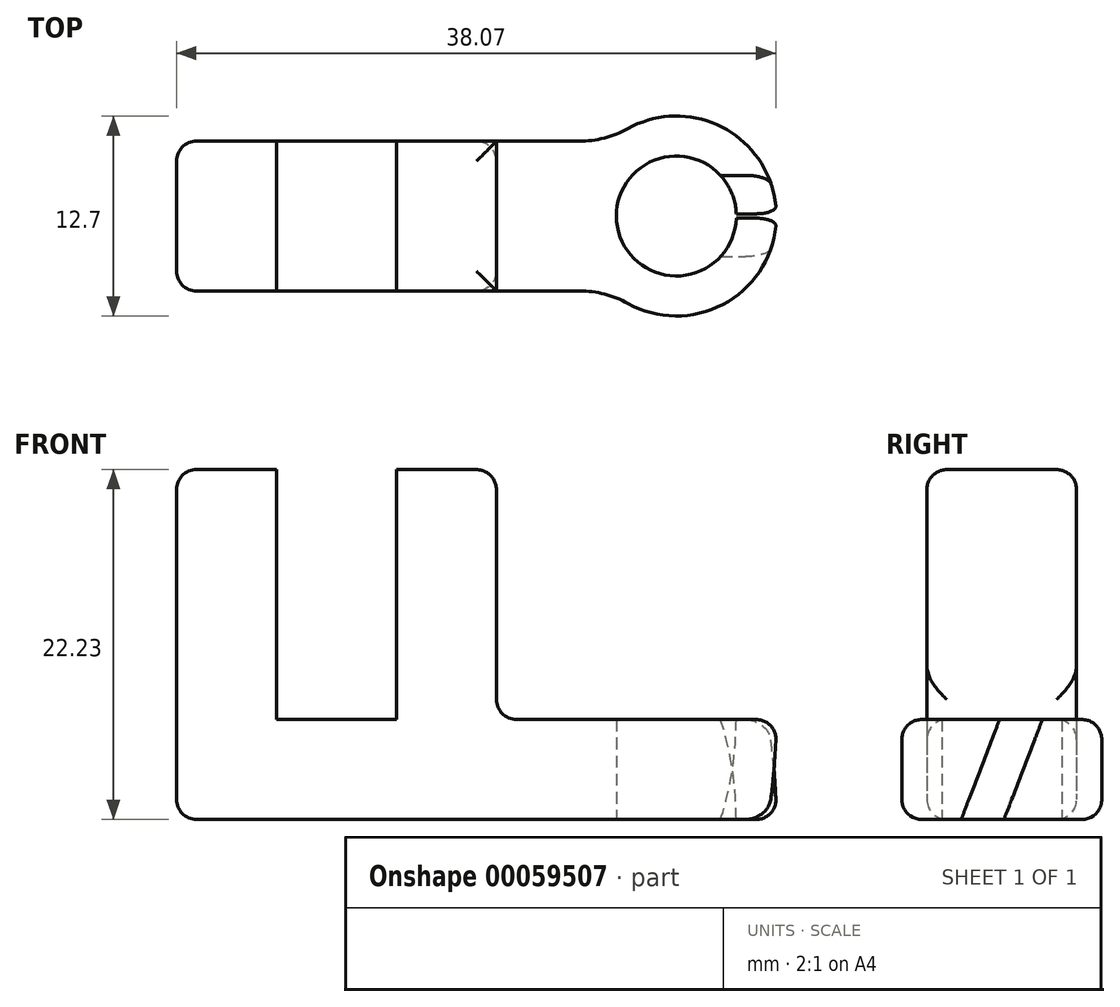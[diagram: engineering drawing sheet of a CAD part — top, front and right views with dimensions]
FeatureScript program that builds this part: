
annotation { "Feature Type Name" : "Feature", "Feature Type Description" : "" }
export const myFeature = defineFeature(function(context is Context, id is Id, definition is map)
    precondition{}
    {
        {
            var Q0;
            Q0=qCreatedBy(makeId("Top.planeOp"),FACE);
            var sketch = newSketch(context, id + "F0", { "sketchPlane" : qUnion([Q0])});
            skArc(sketch, "E0", {"start": v(-3.07, -5.56) * mm, "mid": v(6.35, 0) * mm, "end": v(-3.09, 5.55) * mm});
            skCircle(sketch, "E1", {"center": v(0, 0) * mm, "radius": 3.81 * mm});
            skLineSegment(sketch, "E2", {"start": v(0, 0) * mm, "end": v(-31.75, 0) * mm, "construction": true});
            skLineSegment(sketch, "E3.0", {"start": v(-6.17, 4.75) * mm, "end": v(-31.75, 4.75) * mm});
            skLineSegment(sketch, "E4.0", {"start": v(-6.15, -4.76) * mm, "end": v(-31.75, -4.76) * mm});
            skLineSegment(sketch, "E5", {"start": v(-31.75, 4.75) * mm, "end": v(-31.75, -4.76) * mm});
            skPoint(sketch, "E6.visualSharp", {"position": v(-4.21, 4.75) * mm});
            skArc(sketch, "E6.filletArc", {"start": v(-6.17, 4.75) * mm, "mid": v(-4.58, 4.95) * mm, "end": v(-3.09, 5.55) * mm});
            skPoint(sketch, "E7.visualSharp", {"position": v(-4.2, -4.76) * mm});
            skArc(sketch, "E7.filletArc", {"start": v(-3.07, -5.56) * mm, "mid": v(-4.56, -4.96) * mm, "end": v(-6.15, -4.76) * mm});
            skSolve(sketch);
        }
        {
            var Q0;
            Q0=makeQuery(id+"F0.imprint","IMPRINT",FACE,{"disambiguationData":[TD([[makeQuery(id+"F0.imprint","IMPRINT",EDGE,{"derivedFrom":sQuery(id+"F0.wireOp",EDGE,"E0")}),1.0]])]});
            extrude(context, id + "F1", {"entities" : qUnion([Q0]), "depth" : 6.35 * mm});
        }
        {
            var Q0;
            Q0=makeQuery(id+"F1.opExtrude","CAP_FACE",FACE,{"disambiguationData":[OSD([sQuery(id+"F0.wireOp",EDGE,"E0"),sQuery(id+"F0.wireOp",EDGE,"E1"),sQuery(id+"F0.wireOp",EDGE,"E3.0"),sQuery(id+"F0.wireOp",EDGE,"E4.0"),sQuery(id+"F0.wireOp",EDGE,"E5"),sQuery(id+"F0.wireOp",EDGE,"E6.filletArc"),sQuery(id+"F0.wireOp",EDGE,"E7.filletArc")])],"isStart":false});
            var sketch = newSketch(context, id + "F2", { "sketchPlane" : qUnion([Q0])});
            skLineSegment(sketch, "E8.0", {"start": v(-25.4, 4.75) * mm, "end": v(-25.4, -4.76) * mm});
            skLineSegment(sketch, "E9.0", {"start": v(-17.78, 4.75) * mm, "end": v(-17.78, -4.76) * mm});
            skLineSegment(sketch, "E10.0", {"start": v(-11.43, 4.75) * mm, "end": v(-11.43, -4.76) * mm});
            skSolve(sketch);
        }
        {
            var Q0;
            {var subQ0=sQuery(id+"F2.wireOp",EDGE,"E8.0");Q0=makeQuery(id+"F2.imprint","IMPRINT",FACE,{"disambiguationData":[TD([[makeQuery(id+"F2.imprint","IMPRINT",EDGE,{"derivedFrom":subQ0}),-1.0]])]});}
            var Q1;
            {var subQ0=sQuery(id+"F2.wireOp",EDGE,"E9.0");Q1=makeQuery(id+"F2.imprint","IMPRINT",FACE,{"disambiguationData":[TD([[makeQuery(id+"F2.imprint","IMPRINT",EDGE,{"derivedFrom":subQ0}),1.0]])]});}
            extrude(context, id + "F3", {"entities" : qUnion([Q0, Q1]), "operationType" : NewBodyOperationType.ADD, "depth" : 15.88 * mm});
        }
        {
            var Q0;
            Q0=makeQuery(id+"F1.opExtrude","CAP_EDGE",EDGE,{"disambiguationData":[OSD([sQuery(id+"F0.wireOp",EDGE,"E4.0")])],"isStart":true});
            var Q1;
            {var subQ1=sQuery(id+"F0.wireOp",EDGE,"E4.0");var subQ2=makeQuery(id+"F1.opExtrude","CAP_EDGE",EDGE,{"disambiguationData":[OSD([subQ1])],"isStart":false});var subQ3=sQuery(id+"F0.wireOp",EDGE,"E7.filletArc");Q1=makeQuery(id+"F3.boolean.opBoolean","SPLIT",EDGE,{"disambiguationData":[TD([makeQuery(id+"F1.opExtrude","SWEPT_FACE",FACE,{"disambiguationData":[OSD([subQ3])]})])],"derivedFrom":subQ2});}
            var Q2;
            Q2=makeQuery(id+"F3.opExtrude","CAP_EDGE",EDGE,{"disambiguationData":[OSD([sQuery(id+"F2.wireOp",EDGE,"E10.0")])],"isStart":true});
            var Q3;
            Q3=makeQuery(id+"F3.opExtrude","CAP_EDGE",EDGE,{"disambiguationData":[OSD([sQuery(id+"F2.wireOp",EDGE,"E10.0")])],"isStart":false});
            var Q4;
            {var subQ0=sQuery(id+"F0.wireOp",EDGE,"E5");var subQ1=sQuery(id+"F0.wireOp",EDGE,"E4.0");Q4=makeQuery(id+"F3.boolean.opBoolean","MERGE",EDGE,{"derivedFrom":[makeQuery(id+"F1.opExtrude","SWEPT_EDGE",EDGE,{"disambiguationData":[OSD([subQ1,subQ0])]}),makeQuery(id+"F3.opExtrude","SWEPT_EDGE",EDGE,{"disambiguationData":[OSD([subQ1,subQ0])]})]});}
            var Q5;
            Q5=makeQuery(id+"F1.opExtrude","CAP_EDGE",EDGE,{"disambiguationData":[OSD([sQuery(id+"F0.wireOp",EDGE,"E5")])],"isStart":true});
            var Q6;
            {var subQ0=sQuery(id+"F0.wireOp",EDGE,"E5");var subQ1=sQuery(id+"F0.wireOp",EDGE,"E3.0");Q6=makeQuery(id+"F3.boolean.opBoolean","MERGE",EDGE,{"derivedFrom":[makeQuery(id+"F1.opExtrude","SWEPT_EDGE",EDGE,{"disambiguationData":[OSD([subQ1,subQ0])]}),makeQuery(id+"F3.opExtrude","SWEPT_EDGE",EDGE,{"disambiguationData":[OSD([subQ1,subQ0])]})]});}
            var Q7;
            {var subQ0=sQuery(id+"F0.wireOp",EDGE,"E4.0");var subQ1=makeQuery(id+"F1.opExtrude","CAP_EDGE",EDGE,{"disambiguationData":[OSD([subQ0])],"isStart":false});Q7=makeQuery(id+"F3.opExtrude","CAP_EDGE",EDGE,{"disambiguationData":[OSD([subQ0]),TDD([makeQuery(id+"F2.imprint","IMPRINT",EDGE,{"disambiguationData":[TD([[makeQuery(id+"F2.imprint","INTERSECT",VERTEX,{"derivedFrom":[subQ1,makeQuery(id+"F1.opExtrude","CAP_EDGE",EDGE,{"disambiguationData":[OSD([sQuery(id+"F0.wireOp",EDGE,"E5")])],"isStart":false})]}),1.0]])],"derivedFrom":subQ1})])],"isStart":false});}
            var Q8;
            Q8=makeQuery(id+"F3.opExtrude","CAP_EDGE",EDGE,{"disambiguationData":[OSD([sQuery(id+"F0.wireOp",EDGE,"E5")])],"isStart":false});
            var Q9;
            {var subQ0=sQuery(id+"F0.wireOp",EDGE,"E3.0");var subQ1=makeQuery(id+"F1.opExtrude","CAP_EDGE",EDGE,{"disambiguationData":[OSD([subQ0])],"isStart":false});Q9=makeQuery(id+"F3.opExtrude","CAP_EDGE",EDGE,{"disambiguationData":[OSD([subQ0]),TDD([makeQuery(id+"F2.imprint","IMPRINT",EDGE,{"disambiguationData":[TD([[makeQuery(id+"F2.imprint","INTERSECT",VERTEX,{"derivedFrom":[subQ1,makeQuery(id+"F1.opExtrude","CAP_EDGE",EDGE,{"disambiguationData":[OSD([sQuery(id+"F0.wireOp",EDGE,"E5")])],"isStart":false})]}),1.0]])],"derivedFrom":subQ1})])],"isStart":false});}
            var Q10;
            {var subQ0=sQuery(id+"F0.wireOp",EDGE,"E4.0");var subQ1=makeQuery(id+"F1.opExtrude","CAP_EDGE",EDGE,{"disambiguationData":[OSD([subQ0])],"isStart":false});Q10=makeQuery(id+"F3.opExtrude","CAP_EDGE",EDGE,{"disambiguationData":[OSD([subQ0]),TDD([makeQuery(id+"F2.imprint","IMPRINT",EDGE,{"disambiguationData":[TD([[makeQuery(id+"F2.imprint","INTERSECT",VERTEX,{"derivedFrom":[subQ1,sQuery(id+"F2.wireOp",EDGE,"E9.0")]}),1.0]])],"derivedFrom":subQ1})])],"isStart":false});}
            var Q11;
            {var subQ0=sQuery(id+"F0.wireOp",EDGE,"E3.0");var subQ1=makeQuery(id+"F1.opExtrude","CAP_EDGE",EDGE,{"disambiguationData":[OSD([subQ0])],"isStart":false});Q11=makeQuery(id+"F3.opExtrude","CAP_EDGE",EDGE,{"disambiguationData":[OSD([subQ0]),TDD([makeQuery(id+"F2.imprint","IMPRINT",EDGE,{"disambiguationData":[TD([[makeQuery(id+"F2.imprint","INTERSECT",VERTEX,{"derivedFrom":[subQ1,sQuery(id+"F2.wireOp",EDGE,"E9.0")]}),1.0]])],"derivedFrom":subQ1})])],"isStart":false});}
            fillet(context, id + "F4", {"entities" : qUnion([Q0, Q1, Q2, Q3, Q4, Q5, Q6, Q7, Q8, Q9, Q10, Q11]), "radius" : 1.27 * mm, "tangentPropagation" : true, "allowEdgeOverflow" : false});
        }
        {
            var Q0;
            Q0=qCreatedBy(makeId("Right.planeOp"),FACE);
            var sketch = newSketch(context, id + "F5", { "sketchPlane" : qUnion([Q0])});
            skLineSegment(sketch, "E11.0", {"start": v(-1.99, -5.54) * mm, "end": v(4.36, 10.97) * mm});
            skLineSegment(sketch, "E12.0", {"start": v(-4.36, -4.62) * mm, "end": v(1.99, 11.89) * mm});
            skLineSegment(sketch, "E13", {"start": v(4.36, 10.97) * mm, "end": v(1.99, 11.89) * mm});
            skLineSegment(sketch, "E14", {"start": v(-4.36, -4.62) * mm, "end": v(-1.99, -5.54) * mm});
            skSolve(sketch);
        }
        {
            var Q0;
            Q0=makeQuery(id+"F5.imprint","IMPRINT",FACE,{"disambiguationData":[TD([[makeQuery(id+"F5.imprint","IMPRINT",EDGE,{"derivedFrom":sQuery(id+"F5.wireOp",EDGE,"E11.0")}),1.0]])]});
            extrude(context, id + "F6", {"entities" : qUnion([Q0]), "operationType" : NewBodyOperationType.REMOVE, "endBound" : BoundingType.THROUGH_ALL, "depth" : 25.4 * mm});
        }
    });
